# Revit family: Haworth_HC1Pedestal_13HE_EU_PRELIMINARY
name_source: partatom
category: Furniture Systems
units: mm (PartAtom-declared; Revit-internal decimal feet)

## family parameters
Always vertical = Yes
Cut with Voids When Loaded = No
OmniClass Number = 23.40.70.14.64.21
OmniClass Title = Systems Furniture
Part Type = Normal
Room Calculation Point = No
Round Connector Dimension = Use Diameter
Shared = No
Work Plane-Based = No

## types (2) — shared parameters
Actual Depth = 80 cm
Actual Height = 74 cm
Actual Width = 43 cm
Assembly Code = E2020200
Description = Haworth - HC1 Pedestal - 13HE Pedestal
Glide Finish = Haworth _ Polymer _ Black
Handle 1 = No
Handle 2 = No
Handle Metal = No
Manufacturer = Haworth
Model = MS13081333X
Pull Finish = Haworth _ Paint _ Smooth Plaster
Recessed Handle 128 = No
Recessed Handle 128 Small = No
Revision Number = 1
Size = Verify Final Dim. w/ Haworth
Standard Handle 1 = No
Standard Handle 2 = No
URL = https://www.haworth.com
URL - Product = https://www.haworth.com
Warranty = http://www.haworth.com

## per-type parameters (varying)
| type | Handle 128 128 | High | Large | Low | Small | Thickness | Top Depth | Without Pull |
| 1/3/3/3/6 43.3 x 80 x 74 | No | Yes | Yes | No | No | 3 cm | 90 cm | Yes |
| 1/3/3/3/3 43.3 x 80 x 74 | Yes | No | No | Yes | Yes | 2 cm | 80 cm | No |

## geometry (parser evidence)
native form markers: Sweep x8
no freeform markers — native parametric forms only
